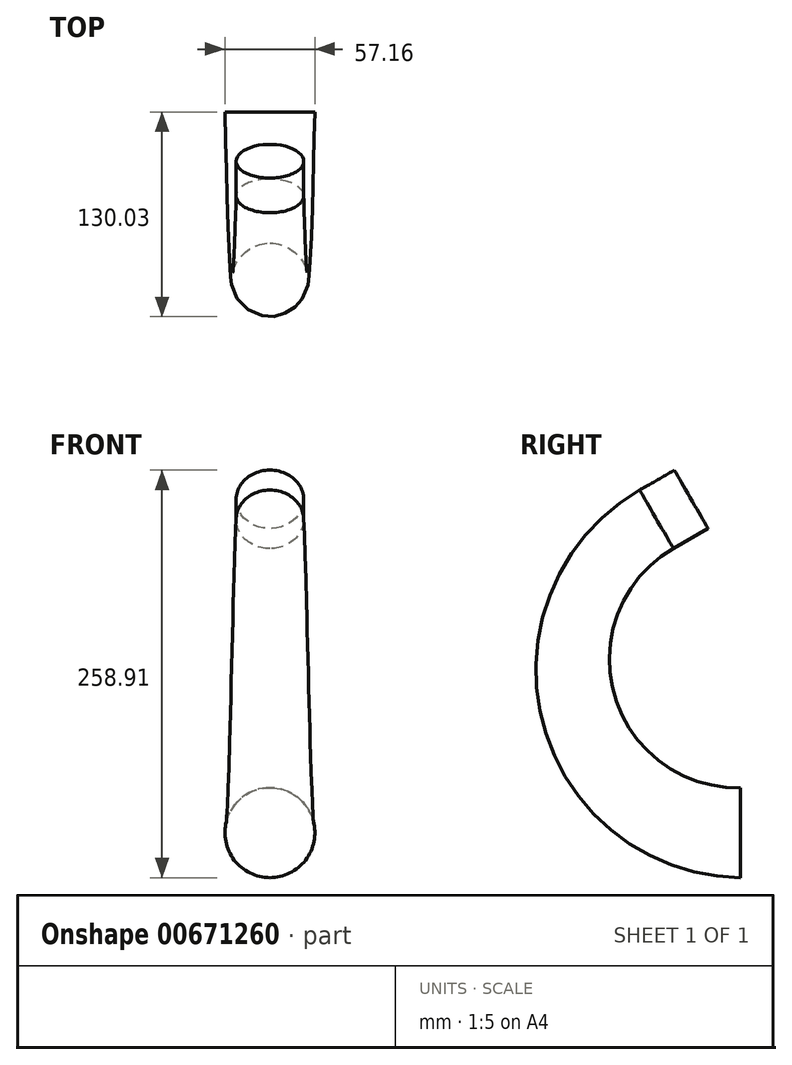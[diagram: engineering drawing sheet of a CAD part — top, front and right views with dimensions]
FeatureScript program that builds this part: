
annotation { "Feature Type Name" : "Feature", "Feature Type Description" : "" }
export const myFeature = defineFeature(function(context is Context, id is Id, definition is map)
    precondition{}
    {
        {
            var Q0;
            Q0=qCreatedBy(makeId("Right.planeOp"),FACE);
            var sketch = newSketch(context, id + "F0", { "sketchPlane" : qUnion([Q0])});
            skLineSegment(sketch, "E0", {"start": v(0, 0) * mm, "end": v(171.45, 0) * mm, "construction": true});
            skLineSegment(sketch, "E1", {"start": v(171.45, 0) * mm, "end": v(339.72, 0) * mm, "construction": true});
            skLineSegment(sketch, "E2", {"start": v(339.72, 0) * mm, "end": v(530.22, 0) * mm, "construction": true});
            skLineSegment(sketch, "E3", {"start": v(530.22, 0) * mm, "end": v(695.32, 0) * mm, "construction": true});
            skLineSegment(sketch, "E4", {"start": v(695.32, 0) * mm, "end": v(1025.53, 0) * mm, "construction": true});
            skLineSegment(sketch, "E5", {"start": v(0, 0) * mm, "end": v(-304.8, 0) * mm, "construction": true});
            skLineSegment(sketch, "E6", {"start": v(0, -28.58) * mm, "end": v(0, 28.58) * mm, "construction": true});
            skLineSegment(sketch, "E7", {"start": v(0, 28.58) * mm, "end": v(-12.7, 0) * mm, "construction": true});
            skLineSegment(sketch, "E8", {"start": v(12.7, 0) * mm, "end": v(0, 28.58) * mm, "construction": true});
            skLineSegment(sketch, "E9", {"start": v(-12.7, 0) * mm, "end": v(0, 0) * mm, "construction": true});
            skLineSegment(sketch, "E10", {"start": v(12.7, 0) * mm, "end": v(0, 0) * mm, "construction": true});
            skLineSegment(sketch, "E11", {"start": v(171.45, 34.13) * mm, "end": v(171.45, -34.13) * mm, "construction": true});
            skLineSegment(sketch, "E12", {"start": v(171.45, 34.13) * mm, "end": v(158.75, 0) * mm, "construction": true});
            skLineSegment(sketch, "E13", {"start": v(158.75, 0) * mm, "end": v(171.45, 0) * mm, "construction": true});
            skLineSegment(sketch, "E14", {"start": v(171.45, 34.13) * mm, "end": v(184.15, 0) * mm, "construction": true});
            skLineSegment(sketch, "E15", {"start": v(184.15, 0) * mm, "end": v(171.45, 0) * mm, "construction": true});
            skLineSegment(sketch, "E16", {"start": v(339.72, 0) * mm, "end": v(327.03, 0) * mm, "construction": true});
            skLineSegment(sketch, "E17", {"start": v(327.02, 0) * mm, "end": v(339.72, 44.45) * mm, "construction": true});
            skLineSegment(sketch, "E18", {"start": v(339.72, 44.45) * mm, "end": v(339.72, -44.45) * mm, "construction": true});
            skLineSegment(sketch, "E19", {"start": v(352.43, 0) * mm, "end": v(339.72, 0) * mm, "construction": true});
            skLineSegment(sketch, "E20", {"start": v(339.73, 44.45) * mm, "end": v(352.43, 0) * mm, "construction": true});
            skLineSegment(sketch, "E21", {"start": v(517.52, 0) * mm, "end": v(530.22, 44.45) * mm, "construction": true});
            skLineSegment(sketch, "E22", {"start": v(530.22, 44.45) * mm, "end": v(530.22, -44.45) * mm, "construction": true});
            skLineSegment(sketch, "E23", {"start": v(530.22, 44.45) * mm, "end": v(542.92, 0) * mm, "construction": true});
            skLineSegment(sketch, "E24", {"start": v(542.92, 0) * mm, "end": v(530.22, 0) * mm, "construction": true});
            skLineSegment(sketch, "E25", {"start": v(530.23, 0) * mm, "end": v(517.52, 0) * mm, "construction": true});
            skLineSegment(sketch, "E26", {"start": v(695.32, 0) * mm, "end": v(682.62, 0) * mm, "construction": true});
            skLineSegment(sketch, "E27", {"start": v(682.62, 0) * mm, "end": v(695.32, 25.4) * mm, "construction": true});
            skLineSegment(sketch, "E28", {"start": v(695.32, 25.4) * mm, "end": v(708.02, 0) * mm, "construction": true});
            skLineSegment(sketch, "E29", {"start": v(695.32, 25.4) * mm, "end": v(695.32, -25.4) * mm, "construction": true});
            skLineSegment(sketch, "E30", {"start": v(695.32, 0) * mm, "end": v(708.02, 0) * mm, "construction": true});
            skLineSegment(sketch, "E31", {"start": v(1025.53, 25.4) * mm, "end": v(1025.53, -25.4) * mm, "construction": true});
            skLineSegment(sketch, "E32", {"start": v(0, 28.58) * mm, "end": v(171.45, 34.13) * mm});
            skLineSegment(sketch, "E33", {"start": v(171.45, 34.13) * mm, "end": v(339.73, 44.45) * mm});
            skLineSegment(sketch, "E34", {"start": v(339.73, 44.45) * mm, "end": v(530.22, 44.45) * mm});
            skLineSegment(sketch, "E35", {"start": v(1025.53, 25.4) * mm, "end": v(695.33, 25.4) * mm});
            skLineSegment(sketch, "E36", {"start": v(0, -28.58) * mm, "end": v(171.45, -34.13) * mm});
            skLineSegment(sketch, "E37", {"start": v(171.45, -34.13) * mm, "end": v(339.72, -44.45) * mm});
            skLineSegment(sketch, "E38", {"start": v(339.72, -44.45) * mm, "end": v(530.22, -44.45) * mm});
            skLineSegment(sketch, "E39", {"start": v(1025.53, -25.4) * mm, "end": v(695.32, -25.4) * mm});
            skLineSegment(sketch, "E40", {"start": v(530.22, 44.45) * mm, "end": v(915.46, 0) * mm, "construction": true});
            skLineSegment(sketch, "E41", {"start": v(915.46, 0) * mm, "end": v(530.22, -44.45) * mm, "construction": true});
            skLineSegment(sketch, "E42", {"start": v(530.22, 44.45) * mm, "end": v(695.33, 25.4) * mm});
            skLineSegment(sketch, "E43", {"start": v(530.22, -44.45) * mm, "end": v(695.32, -25.4) * mm});
            skLineSegment(sketch, "E44", {"start": v(0, 0) * mm, "end": v(0, 106.68) * mm, "construction": true});
            skLineSegment(sketch, "E45", {"start": v(0, 106.68) * mm, "end": v(-53.34, 199.07) * mm, "construction": true});
            skArc(sketch, "E46", {"start": v(0, 0) * mm, "mid": v(-103.04, 79.07) * mm, "end": v(-53.34, 199.07) * mm, "construction": true});
            skLineSegment(sketch, "E47", {"start": v(-53.34, 199.07) * mm, "end": v(-31.34, 211.77) * mm, "construction": true});
            skLineSegment(sketch, "E48", {"start": v(-42.06, 230.33) * mm, "end": v(-20.63, 193.2) * mm, "construction": true});
            skLineSegment(sketch, "E49", {"start": v(-64.06, 217.63) * mm, "end": v(-42.62, 180.5) * mm, "construction": true});
            skLineSegment(sketch, "E50", {"start": v(-64.06, 217.63) * mm, "end": v(-42.06, 230.33) * mm});
            skLineSegment(sketch, "E51", {"start": v(-42.62, 180.5) * mm, "end": v(-20.63, 193.2) * mm});
            skArc(sketch, "E52", {"start": v(-64.06, 217.63) * mm, "mid": v(-125.78, 70.13) * mm, "end": v(0, -28.57) * mm});
            skArc(sketch, "E53", {"start": v(-42.62, 180.5) * mm, "mid": v(-80.31, 87.99) * mm, "end": v(0, 28.58) * mm});
            skLineSegment(sketch, "E54", {"start": v(-279.4, -21.43) * mm, "end": v(-279.4, 21.43) * mm, "construction": true});
            skLineSegment(sketch, "E55", {"start": v(-279.4, 21.43) * mm, "end": v(0, 28.58) * mm, "construction": true});
            skLineSegment(sketch, "E56", {"start": v(0, -28.58) * mm, "end": v(-279.4, -21.43) * mm, "construction": true});
            skLineSegment(sketch, "E57", {"start": v(-279.4, 0) * mm, "end": v(-304.8, 0) * mm, "construction": true});
            skSolve(sketch);
        }
        {
            var Q0;
            Q0=sQuery(id+"F0.wireOp",EDGE,"E49");
            cPlane(context, id + "F1", {"entities" : qUnion([Q0]), "cplaneType" : CPlaneType.LINE_ANGLE, "offset" : 25.4 * mm, "angle" : 90 * degree, "width" : 152.4 * mm, "height" : 152.4 * mm});
        }
        {
            var Q0;
            Q0=qCreatedBy(id+"F1.planeOp",FACE);
            var sketch = newSketch(context, id + "F2", { "sketchPlane" : qUnion([Q0])});
            skLineSegment(sketch, "E58.0", {"start": v(0, 220.5) * mm, "end": v(0, 177.64) * mm, "construction": true});
            skCircle(sketch, "E59", {"center": v(0, 199.07) * mm, "radius": 21.43 * mm});
            skCircle(sketch, "E60.cCircle", {"center": v(0, 199.07) * mm, "radius": 21.43 * mm, "construction": true});
            skLineSegment(sketch, "E60.0", {"start": v(0, 177.64) * mm, "end": v(-6.62, 178.69) * mm, "construction": true});
            skLineSegment(sketch, "E60.1", {"start": v(-6.62, 178.69) * mm, "end": v(-12.6, 181.73) * mm, "construction": true});
            skLineSegment(sketch, "E60.2", {"start": v(-12.6, 181.73) * mm, "end": v(-17.34, 186.47) * mm, "construction": true});
            skLineSegment(sketch, "E60.3", {"start": v(-17.34, 186.47) * mm, "end": v(-20.38, 192.44) * mm, "construction": true});
            skLineSegment(sketch, "E60.4", {"start": v(-20.38, 192.44) * mm, "end": v(-21.43, 199.07) * mm, "construction": true});
            skLineSegment(sketch, "E60.5", {"start": v(-21.43, 199.07) * mm, "end": v(-20.38, 205.7) * mm, "construction": true});
            skLineSegment(sketch, "E60.6", {"start": v(-20.38, 205.7) * mm, "end": v(-17.34, 211.66) * mm, "construction": true});
            skLineSegment(sketch, "E60.7", {"start": v(-17.34, 211.66) * mm, "end": v(-12.6, 216.4) * mm, "construction": true});
            skLineSegment(sketch, "E60.8", {"start": v(-12.6, 216.4) * mm, "end": v(-6.62, 219.45) * mm, "construction": true});
            skLineSegment(sketch, "E60.9", {"start": v(-6.62, 219.45) * mm, "end": v(0, 220.5) * mm, "construction": true});
            skLineSegment(sketch, "E60.10", {"start": v(0, 220.5) * mm, "end": v(6.62, 219.45) * mm, "construction": true});
            skLineSegment(sketch, "E60.11", {"start": v(6.62, 219.45) * mm, "end": v(12.6, 216.4) * mm, "construction": true});
            skLineSegment(sketch, "E60.12", {"start": v(12.6, 216.4) * mm, "end": v(17.34, 211.66) * mm, "construction": true});
            skLineSegment(sketch, "E60.13", {"start": v(17.34, 211.66) * mm, "end": v(20.38, 205.7) * mm, "construction": true});
            skLineSegment(sketch, "E60.14", {"start": v(20.38, 205.7) * mm, "end": v(21.43, 199.07) * mm, "construction": true});
            skLineSegment(sketch, "E60.15", {"start": v(21.43, 199.07) * mm, "end": v(20.38, 192.44) * mm, "construction": true});
            skLineSegment(sketch, "E60.16", {"start": v(20.38, 192.44) * mm, "end": v(17.34, 186.47) * mm, "construction": true});
            skLineSegment(sketch, "E60.17", {"start": v(17.34, 186.47) * mm, "end": v(12.6, 181.73) * mm, "construction": true});
            skLineSegment(sketch, "E60.18", {"start": v(12.6, 181.73) * mm, "end": v(6.62, 178.69) * mm, "construction": true});
            skLineSegment(sketch, "E60.19", {"start": v(6.62, 178.69) * mm, "end": v(0, 177.64) * mm, "construction": true});
            skSolve(sketch);
        }
        {
            var Q0;
            Q0=sQuery(id+"F4.wireOp",EDGE,"E61.0");
            var Q1;
            Q1=sQuery(id+"F0.wireOp",EDGE,"E6");
            cPlane(context, id + "F3", {"entities" : qUnion([Q0, Q1]), "cplaneType" : CPlaneType.LINE_ANGLE, "offset" : 25.4 * mm, "angle" : 90 * degree, "width" : 152.4 * mm, "height" : 152.4 * mm});
        }
        {
            var Q0;
            Q0=qCreatedBy(id+"F3.planeOp",FACE);
            var sketch = newSketch(context, id + "F4", { "sketchPlane" : qUnion([Q0])});
            skLineSegment(sketch, "E61.0", {"start": v(0, -28.58) * mm, "end": v(0, 28.58) * mm, "construction": true});
            skCircle(sketch, "E62", {"center": v(0, 0) * mm, "radius": 28.58 * mm});
            skCircle(sketch, "E63.cCircle", {"center": v(0, 0) * mm, "radius": 28.58 * mm, "construction": true});
            skLineSegment(sketch, "E63.0", {"start": v(0, -28.58) * mm, "end": v(-8.83, -27.18) * mm, "construction": true});
            skLineSegment(sketch, "E63.1", {"start": v(-8.83, -27.18) * mm, "end": v(-16.8, -23.12) * mm, "construction": true});
            skLineSegment(sketch, "E63.2", {"start": v(-16.8, -23.12) * mm, "end": v(-23.12, -16.8) * mm, "construction": true});
            skLineSegment(sketch, "E63.3", {"start": v(-23.12, -16.8) * mm, "end": v(-27.18, -8.83) * mm, "construction": true});
            skLineSegment(sketch, "E63.4", {"start": v(-27.18, -8.83) * mm, "end": v(-28.58, 0) * mm, "construction": true});
            skLineSegment(sketch, "E63.5", {"start": v(-28.58, 0) * mm, "end": v(-27.18, 8.83) * mm, "construction": true});
            skLineSegment(sketch, "E63.6", {"start": v(-27.18, 8.83) * mm, "end": v(-23.12, 16.8) * mm, "construction": true});
            skLineSegment(sketch, "E63.7", {"start": v(-23.12, 16.8) * mm, "end": v(-16.8, 23.12) * mm, "construction": true});
            skLineSegment(sketch, "E63.8", {"start": v(-16.8, 23.12) * mm, "end": v(-8.83, 27.18) * mm, "construction": true});
            skLineSegment(sketch, "E63.9", {"start": v(-8.83, 27.18) * mm, "end": v(0, 28.58) * mm, "construction": true});
            skLineSegment(sketch, "E63.10", {"start": v(0, 28.58) * mm, "end": v(8.83, 27.18) * mm, "construction": true});
            skLineSegment(sketch, "E63.11", {"start": v(8.83, 27.18) * mm, "end": v(16.8, 23.12) * mm, "construction": true});
            skLineSegment(sketch, "E63.12", {"start": v(16.8, 23.12) * mm, "end": v(23.12, 16.8) * mm, "construction": true});
            skLineSegment(sketch, "E63.13", {"start": v(23.12, 16.8) * mm, "end": v(27.18, 8.83) * mm, "construction": true});
            skLineSegment(sketch, "E63.14", {"start": v(27.18, 8.83) * mm, "end": v(28.58, 0) * mm, "construction": true});
            skLineSegment(sketch, "E63.15", {"start": v(28.58, 0) * mm, "end": v(27.18, -8.83) * mm, "construction": true});
            skLineSegment(sketch, "E63.16", {"start": v(27.18, -8.83) * mm, "end": v(23.12, -16.8) * mm, "construction": true});
            skLineSegment(sketch, "E63.17", {"start": v(23.12, -16.8) * mm, "end": v(16.8, -23.12) * mm, "construction": true});
            skLineSegment(sketch, "E63.18", {"start": v(16.8, -23.12) * mm, "end": v(8.83, -27.18) * mm, "construction": true});
            skLineSegment(sketch, "E63.19", {"start": v(8.83, -27.18) * mm, "end": v(0, -28.58) * mm, "construction": true});
            skSolve(sketch);
        }
        {
            var Q0;
            Q0=makeQuery(id+"F2.imprint","IMPRINT",FACE,{"disambiguationData":[TD([[makeQuery(id+"F2.imprint","IMPRINT",EDGE,{"derivedFrom":sQuery(id+"F2.wireOp",EDGE,"E59")}),1.0]])]});
            var Q1;
            Q1=makeQuery(id+"F4.imprint","IMPRINT",FACE,{"disambiguationData":[TD([[makeQuery(id+"F4.imprint","IMPRINT",EDGE,{"derivedFrom":sQuery(id+"F4.wireOp",EDGE,"E62")}),1.0]])]});
            var Q2;
            Q2=sQuery(id+"F0.wireOp",EDGE,"E53");
            var Q3;
            Q3=sQuery(id+"F0.wireOp",EDGE,"E52");
            loft(context, id + "F5", {"addGuides" : true, "sheetProfilesArray" : [{ "sheetProfileEntities" : qUnion([Q0]) }, { "sheetProfileEntities" : qUnion([Q1]) }], "guidesArray" : [{ "guideEntities" : qUnion([Q2]), "guideDerivativeType" : LoftGuideDerivativeType.DEFAULT, "guideDerivativeMagnitude" : 1 }, { "guideEntities" : qUnion([Q3]), "guideDerivativeType" : LoftGuideDerivativeType.DEFAULT, "guideDerivativeMagnitude" : 1 }]});
        }
        {
            var Q0;
            Q0=makeQuery(id+"F2.imprint","IMPRINT",FACE,{"disambiguationData":[TD([[makeQuery(id+"F2.imprint","IMPRINT",EDGE,{"derivedFrom":sQuery(id+"F2.wireOp",EDGE,"E59")}),1.0]])]});
            var Q1;
            Q1=sQuery(id+"F0.wireOp",VERTEX,"E47.end");
            extrude(context, id + "F6", {"entities" : qUnion([Q0]), "operationType" : NewBodyOperationType.ADD, "endBound" : BoundingType.UP_TO_VERTEX, "depth" : 25.4 * mm, "endBoundEntityVertex" : qUnion([Q1]), "offsetDistance" : 25.4 * mm});
        }
    });
